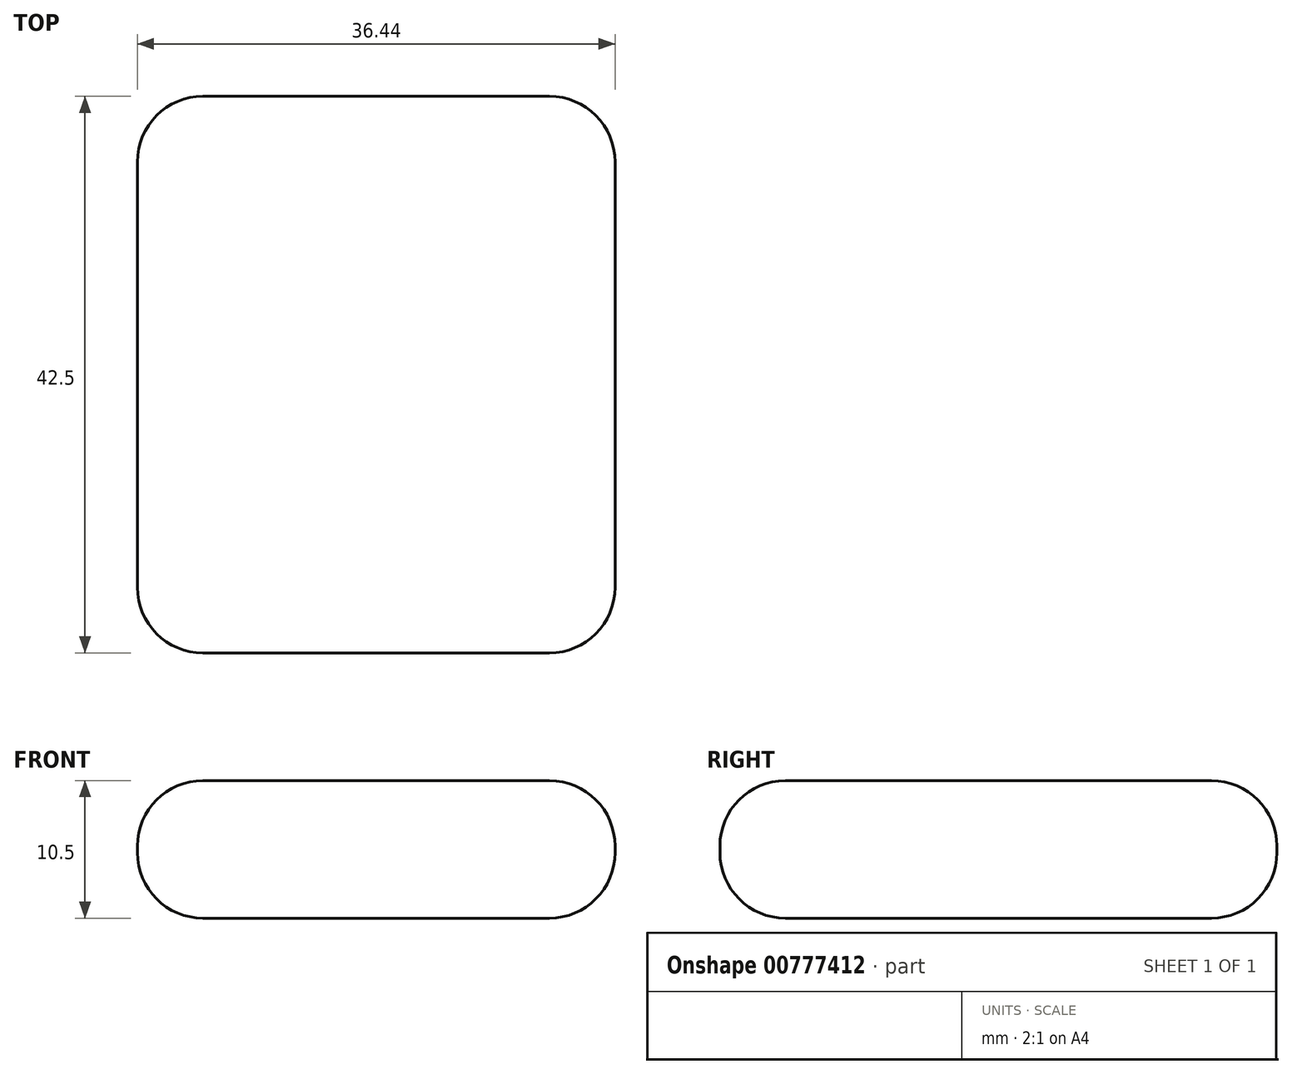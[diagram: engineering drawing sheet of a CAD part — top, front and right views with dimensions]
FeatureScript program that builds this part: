
annotation { "Feature Type Name" : "Feature", "Feature Type Description" : "" }
export const myFeature = defineFeature(function(context is Context, id is Id, definition is map)
    precondition{}
    {
        {
            var Q0;
            Q0=qCreatedBy(makeId("Top.planeOp"),FACE);
            var sketch = newSketch(context, id + "F0", { "sketchPlane" : qUnion([Q0])});
            skLineSegment(sketch, "E0.bottom", {"start": v(-18.22, 21.25) * mm, "end": v(18.22, 21.25) * mm});
            skLineSegment(sketch, "E0.top", {"start": v(-18.22, -21.25) * mm, "end": v(18.22, -21.25) * mm});
            skLineSegment(sketch, "E0.left", {"start": v(-18.22, 21.25) * mm, "end": v(-18.22, -21.25) * mm});
            skLineSegment(sketch, "E0.right", {"start": v(18.22, 21.25) * mm, "end": v(18.22, -21.25) * mm});
            skPoint(sketch, "E0.middle", {"position": v(0, 0) * mm});
            skSolve(sketch);
        }
        {
            var Q0;
            Q0=makeQuery(id+"F0.imprint","IMPRINT",FACE,{"disambiguationData":[TD([[makeQuery(id+"F0.imprint","IMPRINT",EDGE,{"derivedFrom":sQuery(id+"F0.wireOp",EDGE,"E0.bottom")}),-1.0]])]});
            extrude(context, id + "F1", {"entities" : qUnion([Q0]), "endBound" : BoundingType.SYMMETRIC, "depth" : 10.5 * mm, "offsetDistance" : 25 * mm});
        }
        {
            var Q0;
            Q0=makeQuery(id+"F1.opExtrude","CAP_FACE",FACE,{"disambiguationData":[OSD([sQuery(id+"F0.wireOp",EDGE,"E0.bottom"),sQuery(id+"F0.wireOp",EDGE,"E0.top"),sQuery(id+"F0.wireOp",EDGE,"E0.left"),sQuery(id+"F0.wireOp",EDGE,"E0.right")])],"isStart":false});
            var Q1;
            Q1=makeQuery(id+"F1.opExtrude","CAP_EDGE",EDGE,{"disambiguationData":[OSD([sQuery(id+"F0.wireOp",EDGE,"E0.left")])],"isStart":true});
            var Q2;
            Q2=makeQuery(id+"F1.opExtrude","SWEPT_EDGE",EDGE,{"disambiguationData":[OSD([sQuery(id+"F0.wireOp",EDGE,"E0.bottom"),sQuery(id+"F0.wireOp",EDGE,"E0.left")])]});
            var Q3;
            Q3=makeQuery(id+"F1.opExtrude","SWEPT_EDGE",EDGE,{"disambiguationData":[OSD([sQuery(id+"F0.wireOp",EDGE,"E0.top"),sQuery(id+"F0.wireOp",EDGE,"E0.left")])]});
            var Q4;
            Q4=makeQuery(id+"F1.opExtrude","SWEPT_EDGE",EDGE,{"disambiguationData":[OSD([sQuery(id+"F0.wireOp",EDGE,"E0.top"),sQuery(id+"F0.wireOp",EDGE,"E0.right")])]});
            var Q5;
            Q5=makeQuery(id+"F1.opExtrude","SWEPT_EDGE",EDGE,{"disambiguationData":[OSD([sQuery(id+"F0.wireOp",EDGE,"E0.bottom"),sQuery(id+"F0.wireOp",EDGE,"E0.right")])]});
            var Q6;
            Q6=makeQuery(id+"F1.opExtrude","CAP_FACE",FACE,{"disambiguationData":[OSD([sQuery(id+"F0.wireOp",EDGE,"E0.bottom"),sQuery(id+"F0.wireOp",EDGE,"E0.top"),sQuery(id+"F0.wireOp",EDGE,"E0.left"),sQuery(id+"F0.wireOp",EDGE,"E0.right")])],"isStart":true});
            fillet(context, id + "F2", {"entities" : qUnion([Q0, Q1, Q2, Q3, Q4, Q5, Q6]), "radius" : 5 * mm, "tangentPropagation" : true, "allowEdgeOverflow" : false});
        }
    });
